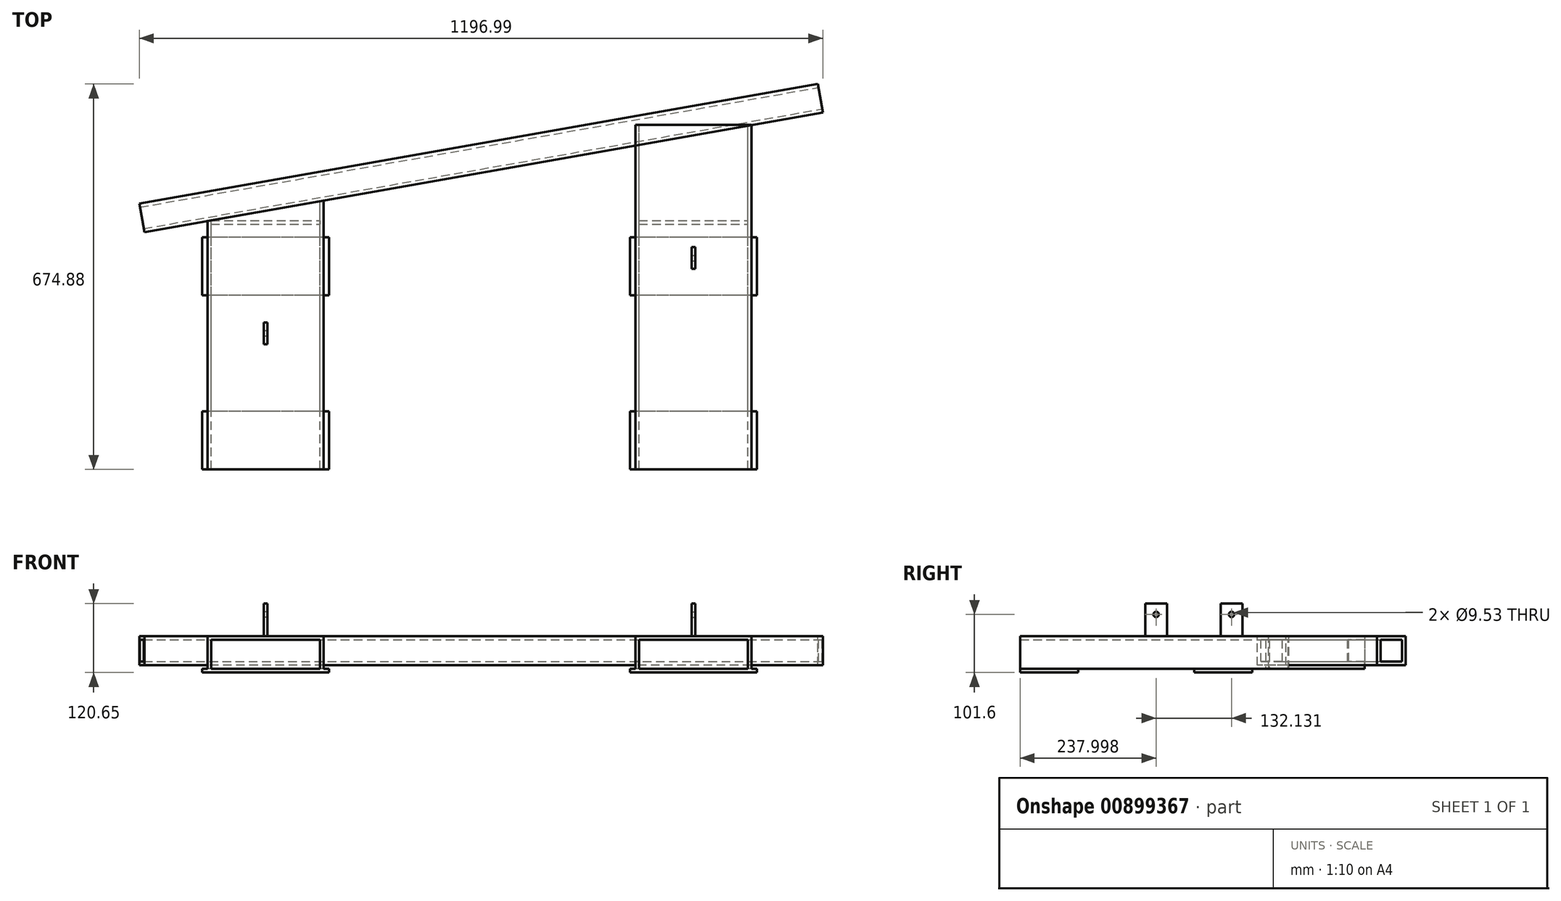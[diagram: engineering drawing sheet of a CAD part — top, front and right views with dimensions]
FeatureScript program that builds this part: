
annotation { "Feature Type Name" : "Feature", "Feature Type Description" : "" }
export const myFeature = defineFeature(function(context is Context, id is Id, definition is map)
    precondition{}
    {
        {
            var Q0;
            Q0=qCreatedBy(makeId("Right.planeOp"),FACE);
            var sketch = newSketch(context, id + "F0", { "sketchPlane" : qUnion([Q0])});
            skLineSegment(sketch, "E0.bottom", {"start": v(-25.4, 25.4) * mm, "end": v(25.4, 25.4) * mm});
            skLineSegment(sketch, "E0.top", {"start": v(-25.4, -25.4) * mm, "end": v(25.4, -25.4) * mm});
            skLineSegment(sketch, "E0.left", {"start": v(-25.4, 25.4) * mm, "end": v(-25.4, -25.4) * mm});
            skLineSegment(sketch, "E0.right", {"start": v(25.4, 25.4) * mm, "end": v(25.4, -25.4) * mm});
            skPoint(sketch, "E0.middle", {"position": v(0, 0) * mm});
            skLineSegment(sketch, "E1.bottom", {"start": v(-19.05, 19.05) * mm, "end": v(19.05, 19.05) * mm});
            skLineSegment(sketch, "E1.top", {"start": v(-19.05, -19.05) * mm, "end": v(19.05, -19.05) * mm});
            skLineSegment(sketch, "E1.left", {"start": v(-19.05, 19.05) * mm, "end": v(-19.05, -19.05) * mm});
            skLineSegment(sketch, "E1.right", {"start": v(19.05, 19.05) * mm, "end": v(19.05, -19.05) * mm});
            skSolve(sketch);
        }
        {
            var Q0;
            Q0=makeQuery(id+"F0.imprint","IMPRINT",FACE,{"disambiguationData":[TD([[makeQuery(id+"F0.imprint","IMPRINT",EDGE,{"derivedFrom":sQuery(id+"F0.wireOp",EDGE,"E0.bottom")}),-1.0]])]});
            extrude(context, id + "F1", {"entities" : qUnion([Q0]), "oppositeDirection" : true, "depth" : 1206.5 * mm, "offsetDistance" : 25.4 * mm});
        }
        {
            var Q0;
            Q0=qCreatedBy(makeId("Front.planeOp"),FACE);
            cPlane(context, id + "F2", {"entities" : qUnion([Q0]), "cplaneType" : CPlaneType.OFFSET, "offset" : 25.4 * mm, "width" : 152.4 * mm, "height" : 152.4 * mm});
        }
        {
            var Q0;
            Q0=qCreatedBy(id+"F2.planeOp",FACE);
            var sketch = newSketch(context, id + "F3", { "sketchPlane" : qUnion([Q0])});
            skLineSegment(sketch, "E2.bottom", {"start": v(-1079.5, 25.4) * mm, "end": v(-876.3, 25.4) * mm});
            skLineSegment(sketch, "E2.top", {"start": v(-1079.5, -31.75) * mm, "end": v(-1073.15, -31.75) * mm});
            skLineSegment(sketch, "E2.left", {"start": v(-1079.5, 25.4) * mm, "end": v(-1079.5, -31.75) * mm});
            skLineSegment(sketch, "E2.right", {"start": v(-876.3, 25.4) * mm, "end": v(-876.3, -31.75) * mm});
            skLineSegment(sketch, "E3.bottom", {"start": v(-127, 25.4) * mm, "end": v(-330.2, 25.4) * mm});
            skLineSegment(sketch, "E3.top", {"start": v(-127, -31.75) * mm, "end": v(-133.35, -31.75) * mm});
            skLineSegment(sketch, "E3.left", {"start": v(-127, 25.4) * mm, "end": v(-127, -31.75) * mm});
            skLineSegment(sketch, "E3.right", {"start": v(-330.2, 25.4) * mm, "end": v(-330.2, -31.75) * mm});
            skLineSegment(sketch, "E4", {"start": v(-1073.15, -31.75) * mm, "end": v(-1073.15, 19.05) * mm});
            skLineSegment(sketch, "E5", {"start": v(-1073.15, 19.05) * mm, "end": v(-882.65, 19.05) * mm});
            skLineSegment(sketch, "E6", {"start": v(-882.65, 19.05) * mm, "end": v(-882.65, -31.75) * mm});
            skLineSegment(sketch, "E7", {"start": v(-323.85, -31.75) * mm, "end": v(-323.85, 19.05) * mm});
            skLineSegment(sketch, "E8", {"start": v(-323.85, 19.05) * mm, "end": v(-133.35, 19.05) * mm});
            skLineSegment(sketch, "E9", {"start": v(-133.35, 19.05) * mm, "end": v(-133.35, -31.75) * mm});
            skLineSegment(sketch, "E10.trimOffspring", {"start": v(-882.65, -31.75) * mm, "end": v(-876.3, -31.75) * mm});
            skLineSegment(sketch, "E11.trimOffspring", {"start": v(-323.85, -31.75) * mm, "end": v(-330.2, -31.75) * mm});
            skSolve(sketch);
        }
        {
            var Q0;
            Q0=qSketchRegion(id+"F3",true);
            extrude(context, id + "F4", {"entities" : qUnion([Q0]), "operationType" : NewBodyOperationType.ADD, "depth" : 603.25 * mm, "offsetDistance" : 25.4 * mm});
        }
        {
            var Q0;
            Q0=makeQuery(id+"F4.opExtrude","SWEPT_FACE",FACE,{"disambiguationData":[OSD([sQuery(id+"F3.wireOp",EDGE,"E10.trimOffspring")])]});
            var sketch = newSketch(context, id + "F5", { "sketchPlane" : qUnion([Q0])});
            skLineSegment(sketch, "E12.bottom", {"start": v(-117.48, 222.25) * mm, "end": v(-339.73, 222.25) * mm});
            skLineSegment(sketch, "E12.top", {"start": v(-117.48, 323.85) * mm, "end": v(-339.73, 323.85) * mm});
            skLineSegment(sketch, "E12.left", {"start": v(-117.48, 222.25) * mm, "end": v(-117.48, 323.85) * mm});
            skLineSegment(sketch, "E12.right", {"start": v(-339.73, 222.25) * mm, "end": v(-339.73, 323.85) * mm});
            skLineSegment(sketch, "E13.bottom", {"start": v(-117.48, 527.05) * mm, "end": v(-339.73, 527.05) * mm});
            skLineSegment(sketch, "E13.top", {"start": v(-117.48, 628.65) * mm, "end": v(-339.73, 628.65) * mm});
            skLineSegment(sketch, "E13.left", {"start": v(-117.48, 527.05) * mm, "end": v(-117.48, 628.65) * mm});
            skLineSegment(sketch, "E13.right", {"start": v(-339.73, 527.05) * mm, "end": v(-339.73, 628.65) * mm});
            skLineSegment(sketch, "E14.bottom", {"start": v(-866.78, 222.25) * mm, "end": v(-1089.03, 222.25) * mm});
            skLineSegment(sketch, "E14.top", {"start": v(-866.78, 323.85) * mm, "end": v(-1089.03, 323.85) * mm});
            skLineSegment(sketch, "E14.left", {"start": v(-866.78, 222.25) * mm, "end": v(-866.78, 323.85) * mm});
            skLineSegment(sketch, "E14.right", {"start": v(-1089.03, 222.25) * mm, "end": v(-1089.03, 323.85) * mm});
            skLineSegment(sketch, "E15.bottom", {"start": v(-866.78, 527.05) * mm, "end": v(-1089.03, 527.05) * mm});
            skLineSegment(sketch, "E15.top", {"start": v(-866.78, 628.65) * mm, "end": v(-1089.03, 628.65) * mm});
            skLineSegment(sketch, "E15.left", {"start": v(-866.78, 527.05) * mm, "end": v(-866.78, 628.65) * mm});
            skLineSegment(sketch, "E15.right", {"start": v(-1089.03, 527.05) * mm, "end": v(-1089.03, 628.65) * mm});
            skSolve(sketch);
        }
        {
            var Q0;
            Q0=qSketchRegion(id+"F5",true);
            extrude(context, id + "F6", {"entities" : qUnion([Q0]), "operationType" : NewBodyOperationType.ADD, "depth" : 6.35 * mm, "offsetDistance" : 25.4 * mm});
        }
        {
            var Q0;
            Q0=makeQuery(id+"F4.boolean.opBoolean","MERGE",FACE,{"derivedFrom":[makeQuery(id+"F1.opExtrude","SWEPT_FACE",FACE,{"disambiguationData":[OSD([sQuery(id+"F0.wireOp",EDGE,"E0.bottom")])]}),makeQuery(id+"F4.opExtrude","SWEPT_FACE",FACE,{"disambiguationData":[OSD([sQuery(id+"F3.wireOp",EDGE,"E2.bottom")])]}),makeQuery(id+"F4.opExtrude","SWEPT_FACE",FACE,{"disambiguationData":[OSD([sQuery(id+"F3.wireOp",EDGE,"E3.bottom")])]})]});
            var sketch = newSketch(context, id + "F7", { "sketchPlane" : qUnion([Q0])});
            skLineSegment(sketch, "E16.bottom", {"start": v(-231.77, -239.47) * mm, "end": v(-225.42, -239.47) * mm});
            skLineSegment(sketch, "E16.top", {"start": v(-231.77, -277.57) * mm, "end": v(-225.42, -277.57) * mm});
            skLineSegment(sketch, "E16.left", {"start": v(-231.77, -239.47) * mm, "end": v(-231.77, -277.57) * mm});
            skLineSegment(sketch, "E16.right", {"start": v(-225.42, -239.47) * mm, "end": v(-225.42, -277.57) * mm});
            skLineSegment(sketch, "E17.bottom", {"start": v(-981.08, -371.6) * mm, "end": v(-974.73, -371.6) * mm});
            skLineSegment(sketch, "E17.top", {"start": v(-981.08, -409.7) * mm, "end": v(-974.73, -409.7) * mm});
            skLineSegment(sketch, "E17.left", {"start": v(-981.08, -371.6) * mm, "end": v(-981.08, -409.7) * mm});
            skLineSegment(sketch, "E17.right", {"start": v(-974.73, -371.6) * mm, "end": v(-974.73, -409.7) * mm});
            skSolve(sketch);
        }
        {
            var Q0;
            Q0=qSketchRegion(id+"F7",true);
            extrude(context, id + "F8", {"entities" : qUnion([Q0]), "operationType" : NewBodyOperationType.ADD, "depth" : 57.15 * mm, "offsetDistance" : 25.4 * mm});
        }
        {
            var Q0;
            Q0=makeQuery(id+"F8.opExtrude","SWEPT_FACE",FACE,{"disambiguationData":[OSD([sQuery(id+"F7.wireOp",EDGE,"E16.right")])]});
            var sketch = newSketch(context, id + "F9", { "sketchPlane" : qUnion([Q0])});
            skCircle(sketch, "E18", {"center": v(-258.52, 63.5) * mm, "radius": 4.76 * mm});
            skSolve(sketch);
        }
        {
            var Q0;
            Q0=qSketchRegion(id+"F9",true);
            extrude(context, id + "F10", {"entities" : qUnion([Q0]), "operationType" : NewBodyOperationType.REMOVE, "oppositeDirection" : true, "depth" : 762 * mm, "offsetDistance" : 25.4 * mm});
        }
        {
            var Q0;
            Q0=makeQuery(id+"F4.boolean.opBoolean","MERGE",FACE,{"derivedFrom":[makeQuery(id+"F1.opExtrude","SWEPT_FACE",FACE,{"disambiguationData":[OSD([sQuery(id+"F0.wireOp",EDGE,"E0.bottom")])]}),makeQuery(id+"F4.opExtrude","SWEPT_FACE",FACE,{"disambiguationData":[OSD([sQuery(id+"F3.wireOp",EDGE,"E2.bottom")])]}),makeQuery(id+"F4.opExtrude","SWEPT_FACE",FACE,{"disambiguationData":[OSD([sQuery(id+"F3.wireOp",EDGE,"E3.bottom")])]})]});
            var sketch = newSketch(context, id + "F11", { "sketchPlane" : qUnion([Q0])});
            skLineSegment(sketch, "E19", {"start": v(-1079.5, -193.35) * mm, "end": v(-1079.5, -25.4) * mm});
            skLineSegment(sketch, "E20", {"start": v(-1079.5, -25.4) * mm, "end": v(-127, -25.4) * mm});
            skLineSegment(sketch, "E21", {"start": v(-1079.5, -25.4) * mm, "end": v(-124.46, -25.4) * mm});
            skLineSegment(sketch, "E22", {"start": v(-124.46, -25.4) * mm, "end": v(-1079.5, -193.8) * mm});
            skLineSegment(sketch, "E23", {"start": v(-1079.5, -193.8) * mm, "end": v(-1079.5, -25.4) * mm});
            skSolve(sketch);
        }
        {
            var Q0;
            {var subQ3=sQuery(id+"F3.wireOp",EDGE,"E2.bottom");var subQ7=makeQuery(id+"F4.opExtrude","SWEPT_EDGE",EDGE,{"disambiguationData":[OSD([subQ3,sQuery(id+"F3.wireOp",EDGE,"E2.right")])]});var subQ9=sQuery(id+"F11.wireOp",EDGE,"E22");var subQ11=makeQuery(id+"F11.imprint","INTERSECT",VERTEX,{"derivedFrom":[subQ7,subQ9]});Q0=makeQuery(id+"F11.imprint","IMPRINT",FACE,{"disambiguationData":[TD([[makeQuery(id+"F11.imprint","IMPRINT",EDGE,{"disambiguationData":[TD([[subQ11,-1.0]])],"derivedFrom":subQ9}),-1.0]])]});}
            var Q1;
            {var subQ0=sQuery(id+"F11.wireOp",EDGE,"E21");var subQ1=sQuery(id+"F3.wireOp",EDGE,"E3.bottom");var subQ2=makeQuery(id+"F4.opExtrude","SWEPT_EDGE",EDGE,{"disambiguationData":[OSD([subQ1,sQuery(id+"F3.wireOp",EDGE,"E3.left")])]});var subQ3=makeQuery(id+"F11.imprint","INTERSECT",VERTEX,{"derivedFrom":[subQ2,subQ0]});Q1=makeQuery(id+"F11.imprint","IMPRINT",FACE,{"disambiguationData":[TD([[makeQuery(id+"F11.imprint","IMPRINT",EDGE,{"disambiguationData":[TD([[subQ3,1.0]])],"derivedFrom":subQ0}),-1.0]])]});}
            var Q2;
            {var subQ0=sQuery(id+"F11.wireOp",EDGE,"E21");var subQ1=makeQuery(id+"F4.opExtrude","SWEPT_EDGE",EDGE,{"disambiguationData":[OSD([sQuery(id+"F3.wireOp",EDGE,"E2.bottom"),sQuery(id+"F3.wireOp",EDGE,"E2.right")])]});var subQ2=makeQuery(id+"F11.imprint","INTERSECT",VERTEX,{"derivedFrom":[subQ1,subQ0]});Q2=makeQuery(id+"F11.imprint","IMPRINT",FACE,{"disambiguationData":[TD([[makeQuery(id+"F11.imprint","IMPRINT",EDGE,{"disambiguationData":[TD([[subQ2,-1.0]])],"derivedFrom":subQ0}),-1.0]])]});}
            extrude(context, id + "F12", {"entities" : qUnion([Q0, Q1, Q2]), "operationType" : NewBodyOperationType.REMOVE, "oppositeDirection" : true, "depth" : 127 * mm, "offsetDistance" : 25.4 * mm});
        }
        {
            var Q0;
            {var subQ1=sQuery(id+"F0.wireOp",EDGE,"E0.left");var subQ7=sQuery(id+"F0.wireOp",EDGE,"E0.bottom");Q0=makeQuery(id+"F12.boolean.opBoolean","SPLIT",FACE,{"disambiguationData":[TD([makeQuery(id+"F1.opExtrude","SWEPT_FACE",FACE,{"disambiguationData":[OSD([subQ1])]})])],"derivedFrom":makeQuery(id+"F4.boolean.opBoolean","MERGE",FACE,{"derivedFrom":[makeQuery(id+"F1.opExtrude","SWEPT_FACE",FACE,{"disambiguationData":[OSD([subQ7])]}),makeQuery(id+"F4.opExtrude","SWEPT_FACE",FACE,{"disambiguationData":[OSD([sQuery(id+"F3.wireOp",EDGE,"E2.bottom")])]}),makeQuery(id+"F4.opExtrude","SWEPT_FACE",FACE,{"disambiguationData":[OSD([sQuery(id+"F3.wireOp",EDGE,"E3.bottom")])]})]})});}
            var sketch = newSketch(context, id + "F13", { "sketchPlane" : qUnion([Q0])});
            skLineSegment(sketch, "E24.bottom", {"start": v(-1219.67, 38.08) * mm, "end": v(23.57, 38.08) * mm});
            skLineSegment(sketch, "E24.top", {"start": v(-1219.67, -25.4) * mm, "end": v(23.57, -25.4) * mm});
            skLineSegment(sketch, "E24.left", {"start": v(-1219.67, 38.08) * mm, "end": v(-1219.67, -25.4) * mm});
            skLineSegment(sketch, "E24.right", {"start": v(23.57, 38.08) * mm, "end": v(23.57, -25.4) * mm});
            skSolve(sketch);
        }
        {
            var Q0;
            Q0=makeQuery(id+"F13.imprint","IMPRINT",FACE,{"disambiguationData":[TD([[makeQuery(id+"F13.imprint","IMPRINT",EDGE,{"derivedFrom":sQuery(id+"F13.wireOp",EDGE,"E24.bottom")}),-1.0]])]});
            var Q1;
            {var subQ1=sQuery(id+"F0.wireOp",EDGE,"E0.bottom");var subQ2=makeQuery(id+"F1.opExtrude","CAP_EDGE",EDGE,{"disambiguationData":[OSD([subQ1])],"isStart":true});Q1=makeQuery(id+"F13.imprint","IMPRINT",FACE,{"disambiguationData":[TD([[makeQuery(id+"F13.imprint","IMPRINT",EDGE,{"derivedFrom":subQ2}),1.0]])]});}
            extrude(context, id + "F14", {"entities" : qUnion([Q0, Q1]), "operationType" : NewBodyOperationType.REMOVE, "oppositeDirection" : true, "depth" : 127 * mm, "offsetDistance" : 25.4 * mm});
        }
        {
            var Q0;
            Q0=makeQuery(id+"F12.boolean.opBoolean","COPY",FACE,{"disambiguationData":[TD([makeQuery(id+"F4.opExtrude","SWEPT_FACE",FACE,{"disambiguationData":[OSD([sQuery(id+"F3.wireOp",EDGE,"E3.top")])]})])],"derivedFrom":makeQuery(id+"F12.opExtrude","SWEPT_FACE",FACE,{"disambiguationData":[OSD([sQuery(id+"F11.wireOp",EDGE,"E22")])]})});
            var sketch = newSketch(context, id + "F15", { "sketchPlane" : qUnion([Q0])});
            skLineSegment(sketch, "E25.bottom", {"start": v(2.56, -25.4) * mm, "end": v(1209.06, -25.4) * mm});
            skLineSegment(sketch, "E25.top", {"start": v(2.56, 25.4) * mm, "end": v(1209.06, 25.4) * mm});
            skLineSegment(sketch, "E25.left", {"start": v(2.56, -25.4) * mm, "end": v(2.56, 25.4) * mm});
            skLineSegment(sketch, "E25.right", {"start": v(1209.06, -25.4) * mm, "end": v(1209.06, 25.4) * mm});
            skSolve(sketch);
        }
        {
            var Q0;
            Q0 = qSketchRegion(id + "F15", true);
            extrude(context, id + "F16", {"entities" : qUnion([Q0]), "depth" : 50.8 * mm, "offsetDistance" : 25.4 * mm});
        }
        {
            var Q0;
            Q0=makeQuery(id+"F16.opExtrude","SWEPT_FACE",FACE,{"disambiguationData":[OSD([sQuery(id+"F15.wireOp",EDGE,"E25.left")])]});
            var sketch = newSketch(context, id + "F17", { "sketchPlane" : qUnion([Q0])});
            skLineSegment(sketch, "E26.bottom", {"start": v(41.05, -19.05) * mm, "end": v(2.95, -19.05) * mm});
            skLineSegment(sketch, "E26.top", {"start": v(41.05, 19.05) * mm, "end": v(2.95, 19.05) * mm});
            skLineSegment(sketch, "E26.left", {"start": v(41.05, -19.05) * mm, "end": v(41.05, 19.05) * mm});
            skLineSegment(sketch, "E26.right", {"start": v(2.95, -19.05) * mm, "end": v(2.95, 19.05) * mm});
            skSolve(sketch);
        }
        {
            var Q0;
            Q0 = qSketchRegion(id + "F17", true);
            extrude(context, id + "F18", {"entities" : qUnion([Q0]), "operationType" : NewBodyOperationType.REMOVE, "oppositeDirection" : true, "depth" : 1270 * mm, "offsetDistance" : 25.4 * mm});
        }
        {
            var Q0;
            {var subQ2=sQuery(id+"F3.wireOp",EDGE,"E2.top");var subQ3=sQuery(id+"F5.wireOp",EDGE,"E14.bottom");Q0=makeQuery(id+"F6.boolean.opBoolean","SPLIT",FACE,{"disambiguationData":[TD([makeQuery(id+"F6.opExtrude","SWEPT_FACE",FACE,{"disambiguationData":[OSD([subQ3])]})])],"derivedFrom":makeQuery(id+"F4.opExtrude","SWEPT_FACE",FACE,{"disambiguationData":[OSD([subQ2])]})});}
            var sketch = newSketch(context, id + "F19", { "sketchPlane" : qUnion([Q0])});
            skLineSegment(sketch, "E27.bottom", {"start": v(-1073.15, 192.68) * mm, "end": v(-882.65, 192.68) * mm});
            skLineSegment(sketch, "E27.top", {"start": v(-1073.15, 199.03) * mm, "end": v(-882.65, 199.03) * mm});
            skLineSegment(sketch, "E27.left", {"start": v(-1073.15, 199.03) * mm, "end": v(-1073.15, 192.68) * mm});
            skLineSegment(sketch, "E27.right", {"start": v(-133.35, 199.03) * mm, "end": v(-133.35, 192.68) * mm});
            skLineSegment(sketch, "E28", {"start": v(-882.65, 192.68) * mm, "end": v(-882.65, 199.03) * mm});
            skLineSegment(sketch, "E29", {"start": v(-323.85, 199.03) * mm, "end": v(-323.85, 192.68) * mm});
            skLineSegment(sketch, "E30.trimOffspring", {"start": v(-323.85, 199.03) * mm, "end": v(-133.35, 199.03) * mm});
            skLineSegment(sketch, "E31.trimOffspring", {"start": v(-323.85, 192.68) * mm, "end": v(-133.35, 192.68) * mm});
            skSolve(sketch);
        }
        {
            var Q0;
            Q0 = qSketchRegion(id + "F19", true);
            var Q1;
            Q1=makeQuery(id+"F4.opExtrude","SWEPT_FACE",FACE,{"disambiguationData":[OSD([sQuery(id+"F3.wireOp",EDGE,"E8")])]});
            extrude(context, id + "F20", {"entities" : qUnion([Q0]), "endBound" : BoundingType.UP_TO_SURFACE, "oppositeDirection" : true, "depth" : 25.4 * mm, "endBoundEntityFace" : qUnion([Q1]), "offsetDistance" : 25.4 * mm});
        }
        {
            var Q0;
            Q0=makeQuery(id+"F8.opExtrude","SWEPT_FACE",FACE,{"disambiguationData":[OSD([sQuery(id+"F7.wireOp",EDGE,"E17.left")])]});
            var sketch = newSketch(context, id + "F21", { "sketchPlane" : qUnion([Q0])});
            skCircle(sketch, "E32", {"center": v(390.65, 63.5) * mm, "radius": 4.76 * mm});
            skSolve(sketch);
        }
        {
            var Q0;
            Q0 = qSketchRegion(id + "F21", true);
            extrude(context, id + "F22", {"entities" : qUnion([Q0]), "operationType" : NewBodyOperationType.REMOVE, "oppositeDirection" : true, "depth" : 25.4 * mm, "offsetDistance" : 25.4 * mm});
        }
    });
